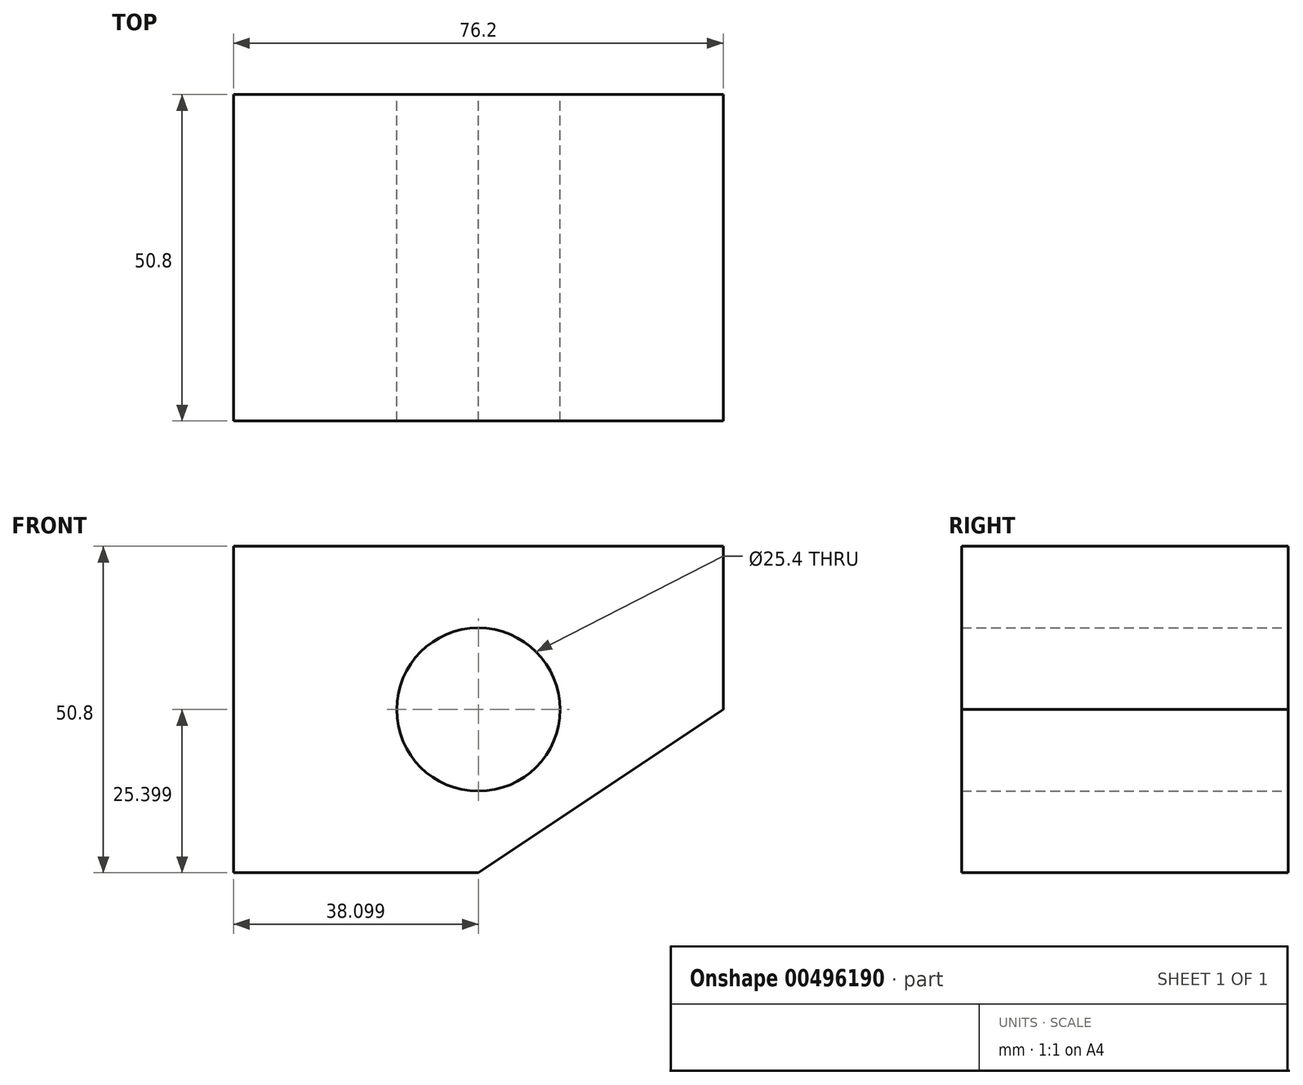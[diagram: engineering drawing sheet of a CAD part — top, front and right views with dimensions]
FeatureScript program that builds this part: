
annotation { "Feature Type Name" : "Feature", "Feature Type Description" : "" }
export const myFeature = defineFeature(function(context is Context, id is Id, definition is map)
    precondition{}
    {
        {
            var Q0;
            Q0=qCreatedBy(makeId("Front.planeOp"),FACE);
            var sketch = newSketch(context, id + "F0", { "sketchPlane" : qUnion([Q0])});
            skLineSegment(sketch, "E0.bottom", {"start": v(12.52, 0.12) * mm, "end": v(-63.68, 0.12) * mm});
            skLineSegment(sketch, "E0.top", {"start": v(-25.58, -50.68) * mm, "end": v(-63.68, -50.68) * mm});
            skLineSegment(sketch, "E0.left", {"start": v(12.52, 0.12) * mm, "end": v(12.52, -25.28) * mm});
            skLineSegment(sketch, "E0.right", {"start": v(-63.68, 0.12) * mm, "end": v(-63.68, -50.68) * mm});
            skPoint(sketch, "E0.middle", {"position": v(-25.58, -25.28) * mm});
            skLineSegment(sketch, "E1", {"start": v(-25.58, -50.68) * mm, "end": v(12.52, -25.28) * mm});
            skPoint(sketch, "E2.orphan", {"position": v(12.52, -50.68) * mm});
            skCircle(sketch, "E3", {"center": v(-25.58, -25.28) * mm, "radius": 12.7 * mm});
            skSolve(sketch);
        }
        {
            var Q0;
            Q0 = qSketchRegion(id + "F0", true);
            extrude(context, id + "F1", {"entities" : qUnion([Q0]), "depth" : 50.8 * mm});
        }
    });
